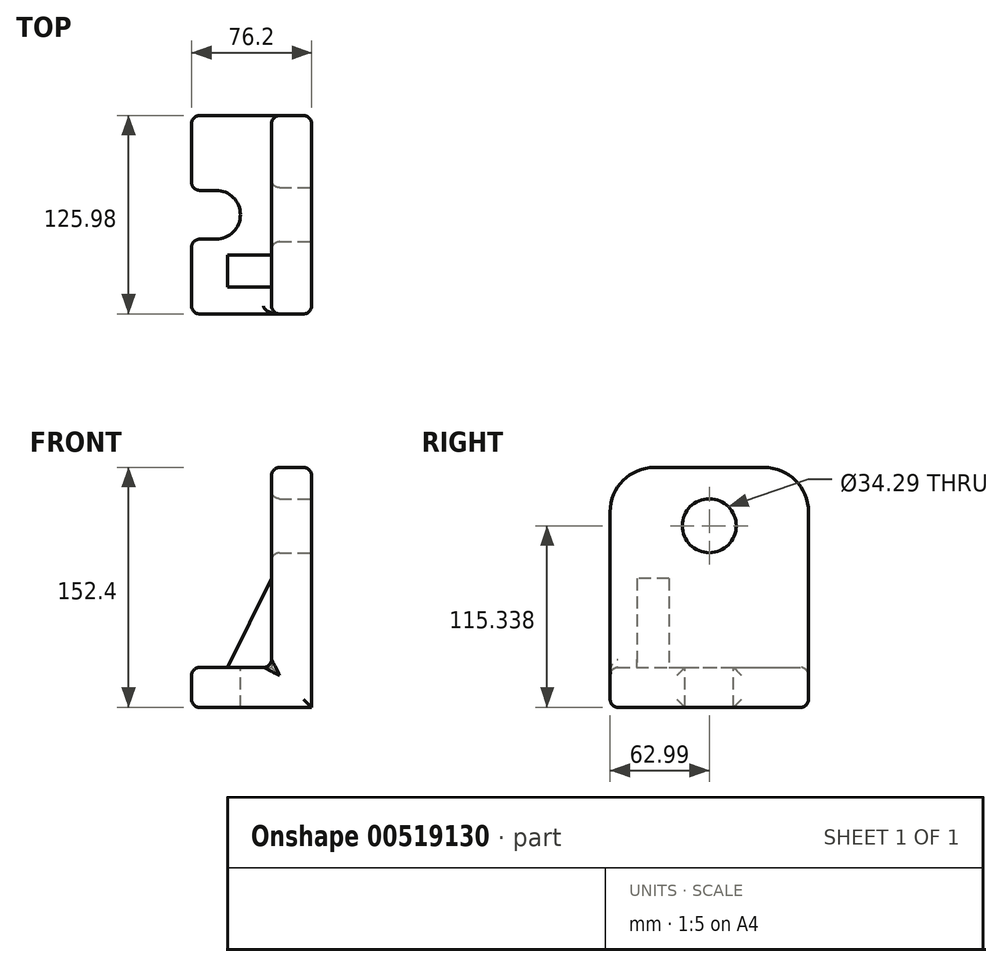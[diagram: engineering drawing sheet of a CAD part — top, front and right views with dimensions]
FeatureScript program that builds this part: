
annotation { "Feature Type Name" : "Feature", "Feature Type Description" : "" }
export const myFeature = defineFeature(function(context is Context, id is Id, definition is map)
    precondition{}
    {
        {
            var Q0;
            Q0=qCreatedBy(makeId("Front.planeOp"),FACE);
            var sketch = newSketch(context, id + "F0", { "sketchPlane" : qUnion([Q0])});
            skLineSegment(sketch, "E0.bottom", {"start": v(0, 0) * mm, "end": v(-76.2, 0) * mm});
            skLineSegment(sketch, "E0.top", {"start": v(0, 152.4) * mm, "end": v(-25.4, 152.4) * mm});
            skLineSegment(sketch, "E0.left", {"start": v(0, 0) * mm, "end": v(0, 152.4) * mm});
            skLineSegment(sketch, "E0.right", {"start": v(-76.2, 0) * mm, "end": v(-76.2, 25.4) * mm});
            skLineSegment(sketch, "E1.top", {"start": v(-76.2, 25.4) * mm, "end": v(-25.4, 25.4) * mm});
            skLineSegment(sketch, "E1.right", {"start": v(-25.4, 152.4) * mm, "end": v(-25.4, 25.4) * mm});
            skSolve(sketch);
        }
        {
            var Q0;
            Q0 = qSketchRegion(id + "F0", true);
            extrude(context, id + "F1", {"entities" : qUnion([Q0]), "depth" : 63 * mm, "offsetDistance" : 25.4 * mm});
        }
        {
            var Q0;
            Q0=makeQuery(id+"F1.opExtrude","SWEPT_BODY",BODY,{"disambiguationData":[OSD([sQuery(id+"F0.wireOp",EDGE,"E0.bottom"),sQuery(id+"F0.wireOp",EDGE,"E0.top"),sQuery(id+"F0.wireOp",EDGE,"E0.left"),sQuery(id+"F0.wireOp",EDGE,"E0.right"),sQuery(id+"F0.wireOp",EDGE,"E1.top"),sQuery(id+"F0.wireOp",EDGE,"E1.right")])]});
            var Q1;
            Q1=qCreatedBy(makeId("Front.planeOp"),FACE);
            mirror(context, id + "F2", {"operationType" : NewBodyOperationType.ADD, "entities" : qUnion([Q0]), "mirrorPlane" : qUnion([Q1])});
        }
        {
            var Q0;
            {var subQ0=makeQuery(id+"F1.opExtrude","SWEPT_FACE",FACE,{"disambiguationData":[OSD([sQuery(id+"F0.wireOp",EDGE,"E1.top")])]});Q0=makeQuery(id+"F2.boolean.opBoolean","MERGE",FACE,{"derivedFrom":[subQ0,makeQuery(id+"F2.opPattern","COPY",FACE,{"derivedFrom":subQ0,"instanceName":"1"})]});}
            var sketch = newSketch(context, id + "F3", { "sketchPlane" : qUnion([Q0])});
            skPoint(sketch, "E2", {"position": v(-60.7, 0) * mm});
            skPoint(sketch, "E2.positionSnap0", {"position": v(-25.4, 0) * mm});
            skCircle(sketch, "E3", {"center": v(-60.7, 0) * mm, "radius": 15.5 * mm});
            skLineSegment(sketch, "E4", {"start": v(-60.7, 15.5) * mm, "end": v(-76.2, 15.5) * mm});
            skPoint(sketch, "E4.endSnap0", {"position": v(-76.2, 0) * mm});
            skLineSegment(sketch, "E5", {"start": v(-60.7, -15.5) * mm, "end": v(-76.2, -15.5) * mm});
            skSolve(sketch);
        }
        {
            var Q0;
            Q0 = qSketchRegion(id + "F3", true);
            var Q1;
            {var subQ0=sQuery(id+"F3.wireOp",EDGE,"E4");Q1=makeQuery(id+"F3.imprint","IMPRINT",FACE,{"disambiguationData":[TD([[makeQuery(id+"F3.imprint","IMPRINT",EDGE,{"derivedFrom":subQ0}),1.0]])]});}
            var Q2;
            {var subQ0=sQuery(id+"F3.wireOp",EDGE,"E5");Q2=makeQuery(id+"F3.imprint","IMPRINT",FACE,{"disambiguationData":[TD([[makeQuery(id+"F3.imprint","IMPRINT",EDGE,{"derivedFrom":subQ0}),-1.0]])]});}
            extrude(context, id + "F4", {"entities" : qUnion([Q0, Q1, Q2]), "operationType" : NewBodyOperationType.REMOVE, "oppositeDirection" : true, "depth" : 75.44 * mm, "offsetDistance" : 25.4 * mm});
        }
        {
            var Q0;
            Q0=qCreatedBy(makeId("Right.planeOp"),FACE);
            var sketch = newSketch(context, id + "F5", { "sketchPlane" : qUnion([Q0])});
            skCircle(sketch, "E6", {"center": v(0, 115.34) * mm, "radius": 17.15 * mm});
            skSolve(sketch);
        }
        {
            var Q0;
            Q0 = qSketchRegion(id + "F5", true);
            extrude(context, id + "F6", {"entities" : qUnion([Q0]), "operationType" : NewBodyOperationType.REMOVE, "oppositeDirection" : true, "depth" : 105.92 * mm, "offsetDistance" : 25.4 * mm});
        }
        {
            var Q0;
            {var subQ0=makeQuery(id+"F1.opExtrude","SWEPT_FACE",FACE,{"disambiguationData":[OSD([sQuery(id+"F0.wireOp",EDGE,"E1.right")])]});Q0=makeQuery(id+"F2.boolean.opBoolean","MERGE",FACE,{"derivedFrom":[subQ0,makeQuery(id+"F2.opPattern","COPY",FACE,{"derivedFrom":subQ0,"instanceName":"1"})]});}
            var sketch = newSketch(context, id + "F7", { "sketchPlane" : qUnion([Q0])});
            skLineSegment(sketch, "E7.bottom", {"start": v(25.7, 81.87) * mm, "end": v(46.03, 81.87) * mm});
            skLineSegment(sketch, "E7.top", {"start": v(25.7, 25.4) * mm, "end": v(46.03, 25.4) * mm});
            skLineSegment(sketch, "E7.left", {"start": v(25.7, 81.87) * mm, "end": v(25.7, 25.4) * mm});
            skLineSegment(sketch, "E7.right", {"start": v(46.03, 81.87) * mm, "end": v(46.03, 25.4) * mm});
            skSolve(sketch);
        }
        {
            var Q0;
            Q0 = qSketchRegion(id + "F7", true);
            extrude(context, id + "F8", {"entities" : qUnion([Q0]), "operationType" : NewBodyOperationType.ADD, "depth" : 27.94 * mm, "offsetDistance" : 25.4 * mm});
        }
        {
            var Q0;
            Q0=makeQuery(id+"F8.opExtrude","SWEPT_FACE",FACE,{"disambiguationData":[OSD([sQuery(id+"F7.wireOp",EDGE,"E7.right")])]});
            var sketch = newSketch(context, id + "F9", { "sketchPlane" : qUnion([Q0])});
            skLineSegment(sketch, "E8", {"start": v(-25.4, 81.87) * mm, "end": v(-53.34, 25.4) * mm});
            skSolve(sketch);
        }
        {
            var Q0;
            Q0 = qSketchRegion(id + "F9", true);
            var Q1;
            Q1=makeQuery(id+"F9.imprint","IMPRINT",FACE,{"disambiguationData":[TD([[makeQuery(id+"F9.imprint","IMPRINT",EDGE,{"derivedFrom":sQuery(id+"F9.wireOp",EDGE,"E8")}),-1.0]])]});
            extrude(context, id + "F10", {"entities" : qUnion([Q0, Q1]), "operationType" : NewBodyOperationType.REMOVE, "oppositeDirection" : true, "depth" : 186.7 * mm, "offsetDistance" : 25.4 * mm});
        }
        {
            var Q0;
            {var subQ0=makeQuery(id+"F1.opExtrude","SWEPT_EDGE",EDGE,{"disambiguationData":[OSD([sQuery(id+"F0.wireOp",EDGE,"E0.top"),sQuery(id+"F0.wireOp",EDGE,"E1.right")])]});Q0=makeQuery(id+"F2.boolean.opBoolean","MERGE",EDGE,{"derivedFrom":[subQ0,makeQuery(id+"F2.opPattern","COPY",EDGE,{"derivedFrom":subQ0,"instanceName":"1"})]});}
            var Q1;
            {var subQ0=makeQuery(id+"F1.opExtrude","SWEPT_EDGE",EDGE,{"disambiguationData":[OSD([sQuery(id+"F0.wireOp",EDGE,"E0.top"),sQuery(id+"F0.wireOp",EDGE,"E0.left")])]});Q1=makeQuery(id+"F2.boolean.opBoolean","MERGE",EDGE,{"derivedFrom":[subQ0,makeQuery(id+"F2.opPattern","COPY",EDGE,{"derivedFrom":subQ0,"instanceName":"1"})]});}
            var Q2;
            Q2=makeQuery(id+"F1.opExtrude","CAP_EDGE",EDGE,{"disambiguationData":[OSD([sQuery(id+"F0.wireOp",EDGE,"E1.right")])],"isStart":false});
            var Q3;
            Q3=makeQuery(id+"F1.opExtrude","CAP_EDGE",EDGE,{"disambiguationData":[OSD([sQuery(id+"F0.wireOp",EDGE,"E0.left")])],"isStart":false});
            var Q4;
            Q4=makeQuery(id+"F1.opExtrude","CAP_EDGE",EDGE,{"disambiguationData":[OSD([sQuery(id+"F0.wireOp",EDGE,"E1.top")])],"isStart":false});
            var Q5;
            Q5=makeQuery(id+"F1.opExtrude","CAP_EDGE",EDGE,{"disambiguationData":[OSD([sQuery(id+"F0.wireOp",EDGE,"E0.bottom")])],"isStart":false});
            var Q6;
            {var subQ0=sQuery(id+"F0.wireOp",EDGE,"E0.right");var subQ2=sQuery(id+"F0.wireOp",EDGE,"E1.top");var subQ4=makeQuery(id+"F1.opExtrude","SWEPT_EDGE",EDGE,{"disambiguationData":[OSD([subQ0,subQ2])]});Q6=makeQuery(id+"F4.boolean.opBoolean","SPLIT",EDGE,{"disambiguationData":[TD([makeQuery(id+"F4.opExtrude","SWEPT_FACE",FACE,{"disambiguationData":[OSD([sQuery(id+"F3.wireOp",EDGE,"E5")])]})])],"derivedFrom":makeQuery(id+"F2.boolean.opBoolean","MERGE",EDGE,{"derivedFrom":[subQ4,makeQuery(id+"F2.opPattern","COPY",EDGE,{"derivedFrom":subQ4,"instanceName":"1"})]})});}
            var Q7;
            {var subQ4=sQuery(id+"F0.wireOp",EDGE,"E0.right");var subQ5=makeQuery(id+"F1.opExtrude","SWEPT_FACE",FACE,{"disambiguationData":[OSD([subQ4])]});Q7=makeQuery(id+"F4.boolean.opBoolean","SPLIT",FACE,{"disambiguationData":[TD([makeQuery(id+"F4.opExtrude","SWEPT_FACE",FACE,{"disambiguationData":[OSD([sQuery(id+"F3.wireOp",EDGE,"E5")])]})])],"derivedFrom":makeQuery(id+"F2.boolean.opBoolean","MERGE",FACE,{"derivedFrom":[subQ5,makeQuery(id+"F2.opPattern","COPY",FACE,{"derivedFrom":subQ5,"instanceName":"1"})]})});}
            var Q8;
            Q8=makeQuery(id+"F4.boolean.opBoolean","COPY",EDGE,{"derivedFrom":makeQuery(id+"F4.opExtrude","CAP_EDGE",EDGE,{"disambiguationData":[OSD([sQuery(id+"F3.wireOp",EDGE,"E3")])],"isStart":true})});
            var Q9;
            Q9=makeQuery(id+"F4.boolean.opBoolean","COPY",EDGE,{"derivedFrom":makeQuery(id+"F4.opExtrude","CAP_EDGE",EDGE,{"disambiguationData":[OSD([sQuery(id+"F3.wireOp",EDGE,"E5")])],"isStart":true})});
            var Q10;
            {var subQ1=sQuery(id+"F0.wireOp",EDGE,"E0.right");var subQ5=makeQuery(id+"F1.opExtrude","SWEPT_FACE",FACE,{"disambiguationData":[OSD([subQ1])]});Q10=makeQuery(id+"F4.boolean.opBoolean","SPLIT",FACE,{"disambiguationData":[TD([makeQuery(id+"F4.opExtrude","SWEPT_FACE",FACE,{"disambiguationData":[OSD([sQuery(id+"F3.wireOp",EDGE,"E4")])]})])],"derivedFrom":makeQuery(id+"F2.boolean.opBoolean","MERGE",FACE,{"derivedFrom":[subQ5,makeQuery(id+"F2.opPattern","COPY",FACE,{"derivedFrom":subQ5,"instanceName":"1"})]})});}
            var Q11;
            Q11=makeQuery(id+"F2.opPattern","COPY",EDGE,{"derivedFrom":makeQuery(id+"F1.opExtrude","CAP_EDGE",EDGE,{"disambiguationData":[OSD([sQuery(id+"F0.wireOp",EDGE,"E1.top")])],"isStart":false}),"instanceName":"1"});
            var Q12;
            Q12=makeQuery(id+"F2.opPattern","COPY",EDGE,{"derivedFrom":makeQuery(id+"F1.opExtrude","CAP_EDGE",EDGE,{"disambiguationData":[OSD([sQuery(id+"F0.wireOp",EDGE,"E0.bottom")])],"isStart":false}),"instanceName":"1"});
            var Q13;
            Q13=makeQuery(id+"F2.opPattern","COPY",EDGE,{"derivedFrom":makeQuery(id+"F1.opExtrude","CAP_EDGE",EDGE,{"disambiguationData":[OSD([sQuery(id+"F0.wireOp",EDGE,"E1.right")])],"isStart":false}),"instanceName":"1"});
            var Q14;
            Q14=makeQuery(id+"F2.opPattern","COPY",EDGE,{"derivedFrom":makeQuery(id+"F1.opExtrude","CAP_EDGE",EDGE,{"disambiguationData":[OSD([sQuery(id+"F0.wireOp",EDGE,"E0.left")])],"isStart":false}),"instanceName":"1"});
            fillet(context, id + "F11", {"entities" : qUnion([Q0, Q1, Q2, Q3, Q4, Q5, Q6, Q7, Q8, Q9, Q10, Q11, Q12, Q13, Q14]), "radius" : 5.08 * mm, "tangentPropagation" : true, "allowEdgeOverflow" : false});
        }
        {
            var Q0;
            Q0=makeQuery(id+"F1.opExtrude","CAP_EDGE",EDGE,{"disambiguationData":[OSD([sQuery(id+"F0.wireOp",EDGE,"E0.top")])],"isStart":false});
            var Q1;
            Q1=makeQuery(id+"F2.opPattern","COPY",EDGE,{"derivedFrom":makeQuery(id+"F1.opExtrude","CAP_EDGE",EDGE,{"disambiguationData":[OSD([sQuery(id+"F0.wireOp",EDGE,"E0.top")])],"isStart":false}),"instanceName":"1"});
            fillet(context, id + "F12", {"entities" : qUnion([Q0, Q1]), "radius" : 28.2 * mm, "tangentPropagation" : true, "allowEdgeOverflow" : false});
        }
        {
            var Q0;
            {var subQ0=makeQuery(id+"F1.opExtrude","SWEPT_FACE",FACE,{"disambiguationData":[OSD([sQuery(id+"F0.wireOp",EDGE,"E1.right")])]});Q0=makeQuery(id+"F6.boolean.opBoolean","INTERSECT",EDGE,{"derivedFrom":[makeQuery(id+"F2.boolean.opBoolean","MERGE",FACE,{"derivedFrom":[subQ0,makeQuery(id+"F2.opPattern","COPY",FACE,{"derivedFrom":subQ0,"instanceName":"1"})]}),makeQuery(id+"F6.opExtrude","SWEPT_FACE",FACE,{"disambiguationData":[OSD([sQuery(id+"F5.wireOp",EDGE,"E6")])]})]});}
            var Q1;
            Q1=makeQuery(id+"F6.boolean.opBoolean","COPY",EDGE,{"derivedFrom":makeQuery(id+"F6.opExtrude","CAP_EDGE",EDGE,{"disambiguationData":[OSD([sQuery(id+"F5.wireOp",EDGE,"E6")])],"isStart":true})});
            fillet(context, id + "F13", {"entities" : qUnion([Q0, Q1]), "radius" : 5.08 * mm, "tangentPropagation" : true, "allowEdgeOverflow" : false});
        }
        {
            var Q0;
            {var subQ0=sQuery(id+"F7.wireOp",EDGE,"E7.top");Q0=makeQuery(id+"F10.boolean.opBoolean","MERGE",EDGE,{"derivedFrom":[makeQuery(id+"F8.opExtrude","CAP_EDGE",EDGE,{"disambiguationData":[OSD([subQ0])],"isStart":false}),makeQuery(id+"F10.opExtrude","SWEPT_EDGE",EDGE,{"disambiguationData":[OSD([sQuery(id+"F0.wireOp",EDGE,"E1.top"),sQuery(id+"F0.wireOp",EDGE,"E1.right"),subQ0,sQuery(id+"F7.wireOp",EDGE,"E7.right"),sQuery(id+"F9.wireOp",EDGE,"E8")])]})]});}
            var Q1;
            {var subQ0=sQuery(id+"F0.wireOp",EDGE,"E1.top");var subQ2=sQuery(id+"F0.wireOp",EDGE,"E1.right");var subQ4=makeQuery(id+"F1.opExtrude","SWEPT_EDGE",EDGE,{"disambiguationData":[OSD([subQ0,subQ2])]});Q1=makeQuery(id+"F8.boolean.opBoolean","SPLIT",EDGE,{"disambiguationData":[TD([makeQuery(id+"F8.opExtrude","SWEPT_FACE",FACE,{"disambiguationData":[OSD([sQuery(id+"F7.wireOp",EDGE,"E7.right")])]})])],"derivedFrom":makeQuery(id+"F2.boolean.opBoolean","MERGE",EDGE,{"derivedFrom":[subQ4,makeQuery(id+"F2.opPattern","COPY",EDGE,{"derivedFrom":subQ4,"instanceName":"1"})]})});}
            var Q2;
            Q2=makeQuery(id+"F8.opExtrude","SWEPT_EDGE",EDGE,{"disambiguationData":[OSD([sQuery(id+"F0.wireOp",EDGE,"E1.top"),sQuery(id+"F0.wireOp",EDGE,"E1.right"),sQuery(id+"F7.wireOp",EDGE,"E7.top"),sQuery(id+"F7.wireOp",EDGE,"E7.right")])]});
            var Q3;
            Q3=makeQuery(id+"F8.opExtrude","SWEPT_EDGE",EDGE,{"disambiguationData":[OSD([sQuery(id+"F0.wireOp",EDGE,"E1.top"),sQuery(id+"F0.wireOp",EDGE,"E1.right"),sQuery(id+"F7.wireOp",EDGE,"E7.top"),sQuery(id+"F7.wireOp",EDGE,"E7.left")])]});
            var Q4;
            Q4=makeQuery(id+"F8.opExtrude","CAP_EDGE",EDGE,{"disambiguationData":[OSD([sQuery(id+"F7.wireOp",EDGE,"E7.right")])],"isStart":true});
            var Q5;
            Q5=makeQuery(id+"F8.opExtrude","CAP_EDGE",EDGE,{"disambiguationData":[OSD([sQuery(id+"F7.wireOp",EDGE,"E7.left")])],"isStart":true});
            fillet(context, id + "F14", {"entities" : qUnion([Q0, Q1, Q2, Q3, Q4, Q5]), "radius" : 5.08 * mm, "tangentPropagation" : true, "allowEdgeOverflow" : false});
        }
    });
